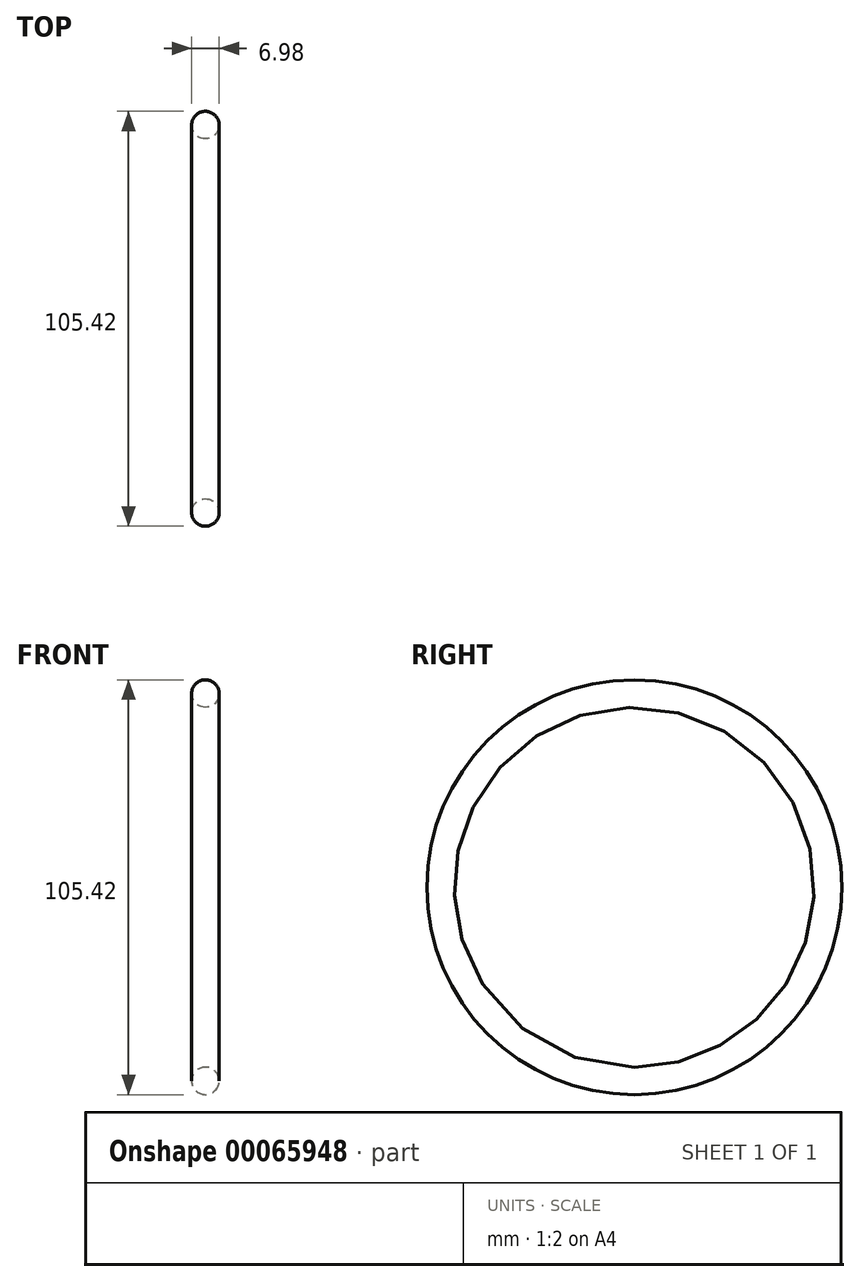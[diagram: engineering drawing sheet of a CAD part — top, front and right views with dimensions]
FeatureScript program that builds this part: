
annotation { "Feature Type Name" : "Feature", "Feature Type Description" : "" }
export const myFeature = defineFeature(function(context is Context, id is Id, definition is map)
    precondition{}
    {
        {
            var Q0;
            Q0=qCreatedBy(makeId("Front.planeOp"),FACE);
            var sketch = newSketch(context, id + "F0", { "sketchPlane" : qUnion([Q0])});
            skLineSegment(sketch, "E0", {"start": v(0, 0) * mm, "end": v(-6.06, 0) * mm, "construction": true});
            skCircle(sketch, "E1", {"center": v(0, 49.21) * mm, "radius": 3.5 * mm});
            skSolve(sketch);
        }
        {
            var Q0;
            Q0=makeQuery(id+"F0.imprint","IMPRINT",FACE,{"disambiguationData":[TD([[makeQuery(id+"F0.imprint","IMPRINT",EDGE,{"derivedFrom":sQuery(id+"F0.wireOp",EDGE,"E1")}),1.0]])]});
            var Q1;
            Q1=sQuery(id+"F0.wireOp",EDGE,"E0");
            revolve(context, id + "F1", {"entities" : qUnion([Q0]), "axis" : qUnion([Q1]), "revolveType" : RevolveType.FULL});
        }
    });
